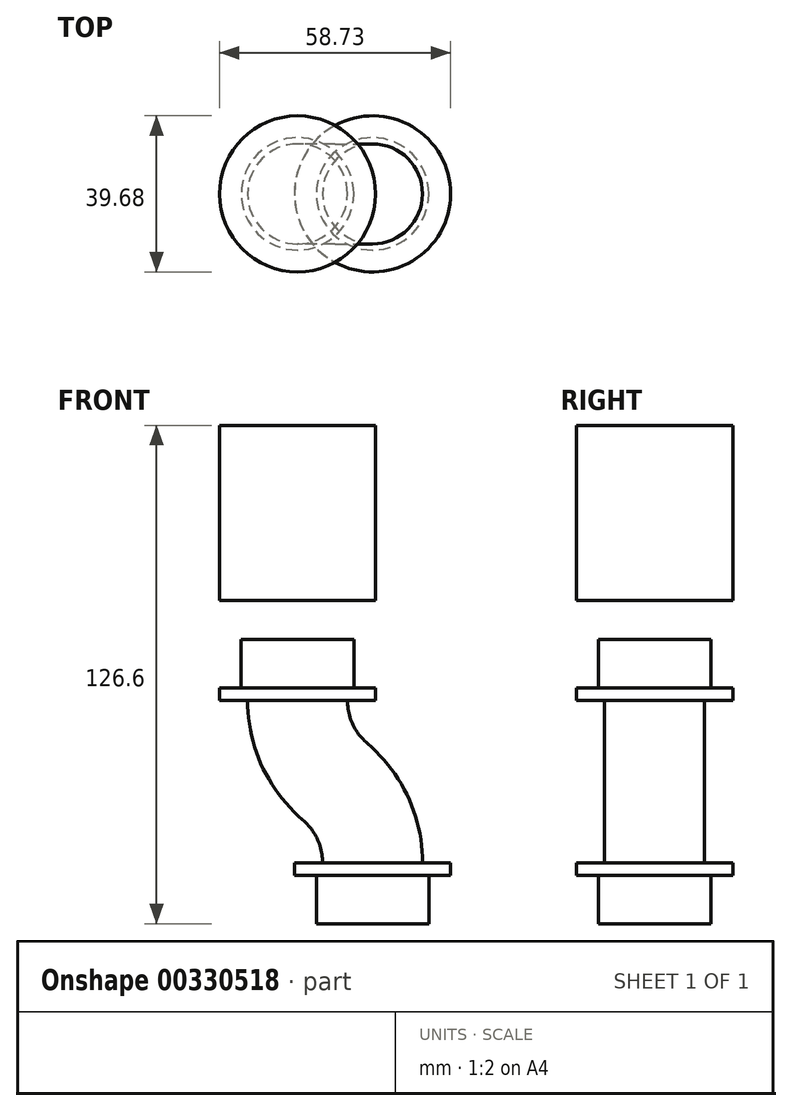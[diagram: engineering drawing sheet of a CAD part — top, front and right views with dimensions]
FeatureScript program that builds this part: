
annotation { "Feature Type Name" : "Feature", "Feature Type Description" : "" }
export const myFeature = defineFeature(function(context is Context, id is Id, definition is map)
    precondition{}
    {
        {
            var Q0;
            Q0=qCreatedBy(makeId("Top.planeOp"),FACE);
            var sketch = newSketch(context, id + "F0", { "sketchPlane" : qUnion([Q0])});
            skCircle(sketch, "E0", {"center": v(0, 0) * mm, "radius": 12.7 * mm});
            skCircle(sketch, "E1", {"center": v(0, 0) * mm, "radius": 19.84 * mm});
            skSolve(sketch);
        }
        {
            var Q0;
            Q0=qCreatedBy(makeId("Top.planeOp"),FACE);
            cPlane(context, id + "F1", {"entities" : qUnion([Q0]), "cplaneType" : CPlaneType.OFFSET, "offset" : 41.27 * mm, "width" : 152.4 * mm, "height" : 152.4 * mm});
        }
        {
            var Q0;
            Q0=qCreatedBy(id+"F1.planeOp",FACE);
            var sketch = newSketch(context, id + "F2", { "sketchPlane" : qUnion([Q0])});
            skCircle(sketch, "E2.0", {"center": v(-19.05, 0) * mm, "radius": 12.7 * mm});
            skCircle(sketch, "E3.0", {"center": v(-19.05, 0) * mm, "radius": 19.84 * mm});
            skSolve(sketch);
        }
        {
            var Q0;
            Q0=qCreatedBy(makeId("Front.planeOp"),FACE);
            var sketch = newSketch(context, id + "F3", { "sketchPlane" : qUnion([Q0])});
            skPoint(sketch, "E4.0", {"position": v(-19.05, 41.28) * mm});
            skPoint(sketch, "E5.0", {"position": v(0, 0) * mm});
            skLineSegment(sketch, "E6", {"start": v(0, 0) * mm, "end": v(0, -22.03) * mm, "construction": true});
            skLineSegment(sketch, "E7", {"start": v(-19.05, 41.28) * mm, "end": v(-19.05, 60.98) * mm, "construction": true});
            skLineSegment(sketch, "E8", {"start": v(-19.05, 41.28) * mm, "end": v(-19.05, 14.54) * mm, "construction": true});
            skLineSegment(sketch, "E9", {"start": v(0, 0) * mm, "end": v(0, 29.01) * mm, "construction": true});
            skArc(sketch, "E10", {"start": v(-19.05, 41.28) * mm, "mid": v(-16.55, 29.91) * mm, "end": v(-9.52, 20.64) * mm});
            skLineSegment(sketch, "E11", {"start": v(-19.05, 20.64) * mm, "end": v(0, 20.64) * mm, "construction": true});
            skLineSegment(sketch, "E12", {"start": v(-9.53, 20.64) * mm, "end": v(-9.53, 39.13) * mm, "construction": true});
            skArc(sketch, "E13.1.0", {"start": v(0, 0) * mm, "mid": v(-2.5, 11.36) * mm, "end": v(-9.53, 20.64) * mm});
            skPoint(sketch, "E13.center", {"position": v(-9.53, 20.64) * mm});
            skSolve(sketch);
        }
        {
            var Q0;
            Q0=makeQuery(id+"F2.imprint","IMPRINT",FACE,{"disambiguationData":[TD([[makeQuery(id+"F2.imprint","IMPRINT",EDGE,{"derivedFrom":sQuery(id+"F2.wireOp",EDGE,"E2.0")}),1.0]])]});
            var Q1;
            Q1=sQuery(id+"F3.wireOp",EDGE,"E10");
            var Q2;
            Q2=sQuery(id+"F3.wireOp",EDGE,"E13.1.0");
            sweep(context, id + "F4", {"profiles" : qUnion([Q0]), "path" : qUnion([Q1, Q2])});
        }
        {
            var Q0;
            Q0=makeQuery(id+"F2.imprint","IMPRINT",FACE,{"disambiguationData":[TD([[makeQuery(id+"F2.imprint","IMPRINT",EDGE,{"derivedFrom":sQuery(id+"F2.wireOp",EDGE,"E2.0")}),1.0]])]});
            var Q1;
            Q1=makeQuery(id+"F2.imprint","IMPRINT",FACE,{"disambiguationData":[TD([[makeQuery(id+"F2.imprint","IMPRINT",EDGE,{"derivedFrom":sQuery(id+"F2.wireOp",EDGE,"E2.0")}),-1.0]])]});
            extrude(context, id + "F5", {"entities" : qUnion([Q0, Q1]), "operationType" : NewBodyOperationType.ADD, "depth" : 3.17 * mm});
        }
        {
            var Q0;
            Q0=makeQuery(id+"F0.imprint","IMPRINT",FACE,{"disambiguationData":[TD([[makeQuery(id+"F0.imprint","IMPRINT",EDGE,{"derivedFrom":sQuery(id+"F0.wireOp",EDGE,"E0")}),-1.0]])]});
            var Q1;
            Q1=makeQuery(id+"F0.imprint","IMPRINT",FACE,{"disambiguationData":[TD([[makeQuery(id+"F0.imprint","IMPRINT",EDGE,{"derivedFrom":sQuery(id+"F0.wireOp",EDGE,"E0")}),1.0]])]});
            extrude(context, id + "F6", {"entities" : qUnion([Q0, Q1]), "operationType" : NewBodyOperationType.ADD, "oppositeDirection" : true, "depth" : 3.17 * mm});
        }
        {
            var Q0;
            Q0=makeQuery(id+"F5.opExtrude","CAP_FACE",FACE,{"disambiguationData":[OSD([sQuery(id+"F2.wireOp",EDGE,"E3.0")])],"isStart":false});
            var sketch = newSketch(context, id + "F7", { "sketchPlane" : qUnion([Q0])});
            skCircle(sketch, "E14", {"center": v(-19.05, 0) * mm, "radius": 14.29 * mm});
            skSolve(sketch);
        }
        {
            var Q0;
            Q0=makeQuery(id+"F7.imprint","IMPRINT",FACE,{"disambiguationData":[TD([[makeQuery(id+"F7.imprint","IMPRINT",EDGE,{"derivedFrom":sQuery(id+"F7.wireOp",EDGE,"E14")}),1.0]])]});
            var Q1;
            Q1=sQuery(id+"F7.wireOp",EDGE,"E14");
            extrude(context, id + "F8", {"entities" : qUnion([Q0]), "operationType" : NewBodyOperationType.ADD, "surfaceEntities" : qUnion([Q1]), "depth" : 12.3 * mm});
        }
        {
            var Q0;
            Q0=makeQuery(id+"F6.opExtrude","CAP_FACE",FACE,{"disambiguationData":[OSD([sQuery(id+"F0.wireOp",EDGE,"E1")])],"isStart":false});
            var sketch = newSketch(context, id + "F9", { "sketchPlane" : qUnion([Q0])});
            skCircle(sketch, "E15", {"center": v(0, 0) * mm, "radius": 14.29 * mm});
            skSolve(sketch);
        }
        {
            var Q0;
            Q0=makeQuery(id+"F9.imprint","IMPRINT",FACE,{"disambiguationData":[TD([[makeQuery(id+"F9.imprint","IMPRINT",EDGE,{"derivedFrom":sQuery(id+"F9.wireOp",EDGE,"E15")}),1.0]])]});
            var Q1;
            Q1=sQuery(id+"F9.wireOp",EDGE,"E15");
            extrude(context, id + "F10", {"entities" : qUnion([Q0]), "operationType" : NewBodyOperationType.ADD, "surfaceEntities" : qUnion([Q1]), "depth" : 12.3 * mm});
        }
        {
            var Q0;
            Q0=qCreatedBy(id+"F1.planeOp",FACE);
            cPlane(context, id + "F11", {"entities" : qUnion([Q0]), "cplaneType" : CPlaneType.OFFSET, "offset" : 25.4 * mm, "width" : 152.4 * mm, "height" : 152.4 * mm});
        }
        {
            var Q0;
            Q0=qCreatedBy(id+"F11.planeOp",FACE);
            var sketch = newSketch(context, id + "F12", { "sketchPlane" : qUnion([Q0])});
            skCircle(sketch, "E16.0", {"center": v(-19.05, 0) * mm, "radius": 19.84 * mm});
            skSolve(sketch);
        }
        {
            var Q0;
            Q0 = qSketchRegion(id + "F12", true);
            extrude(context, id + "F13", {"entities" : qUnion([Q0]), "depth" : 44.45 * mm});
        }
    });
